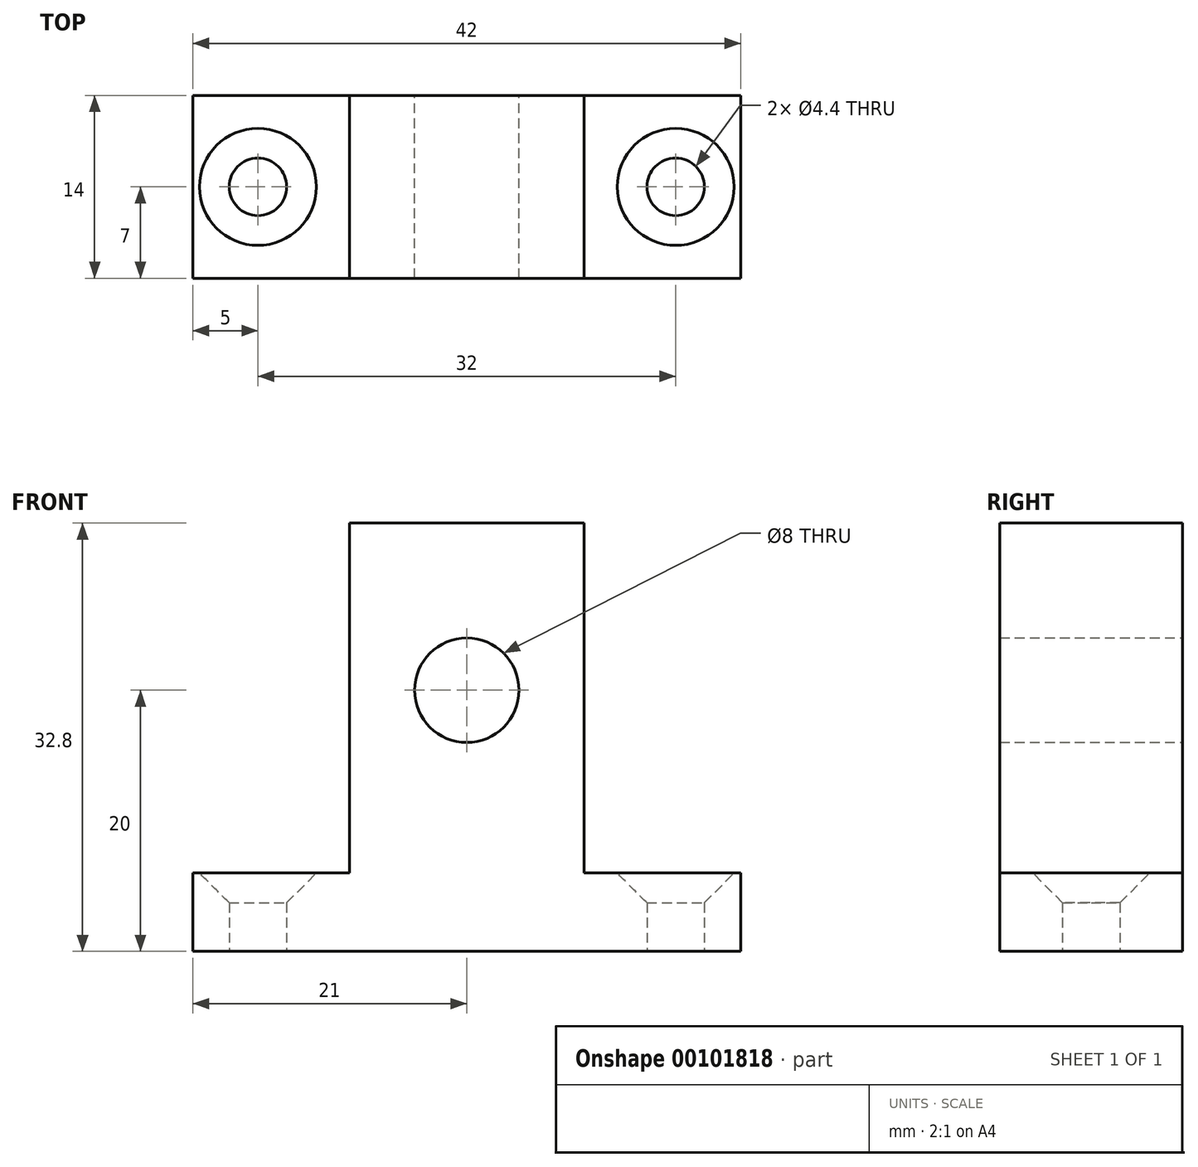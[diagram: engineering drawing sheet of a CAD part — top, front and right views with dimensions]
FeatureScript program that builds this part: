
annotation { "Feature Type Name" : "Feature", "Feature Type Description" : "" }
export const myFeature = defineFeature(function(context is Context, id is Id, definition is map)
    precondition{}
    {
        {
            var Q0;
            Q0=qCreatedBy(makeId("Top.planeOp"),FACE);
            var sketch = newSketch(context, id + "F0", { "sketchPlane" : qUnion([Q0])});
            skLineSegment(sketch, "E0.bottom", {"start": v(-21, 7) * mm, "end": v(21, 7) * mm});
            skLineSegment(sketch, "E0.top", {"start": v(-21, -7) * mm, "end": v(21, -7) * mm});
            skLineSegment(sketch, "E0.left", {"start": v(-21, 7) * mm, "end": v(-21, -7) * mm});
            skLineSegment(sketch, "E0.right", {"start": v(21, 7) * mm, "end": v(21, -7) * mm});
            skPoint(sketch, "E0.middle", {"position": v(0, 0) * mm});
            skSolve(sketch);
        }
        {
            var Q0;
            Q0 = qSketchRegion(id + "F0", true);
            extrude(context, id + "F1", {"entities" : qUnion([Q0]), "depth" : 6 * mm});
        }
        {
            var Q0;
            Q0=makeQuery(id+"F1.opExtrude","CAP_FACE",FACE,{"disambiguationData":[OSD([sQuery(id+"F0.wireOp",EDGE,"E0.bottom"),sQuery(id+"F0.wireOp",EDGE,"E0.top"),sQuery(id+"F0.wireOp",EDGE,"E0.left"),sQuery(id+"F0.wireOp",EDGE,"E0.right")])],"isStart":false});
            var sketch = newSketch(context, id + "F2", { "sketchPlane" : qUnion([Q0])});
            skLineSegment(sketch, "E1.bottom", {"start": v(-9, 7) * mm, "end": v(9, 7) * mm});
            skLineSegment(sketch, "E1.top", {"start": v(-9, -7) * mm, "end": v(9, -7) * mm});
            skLineSegment(sketch, "E1.left", {"start": v(-9, 7) * mm, "end": v(-9, -7) * mm});
            skLineSegment(sketch, "E1.right", {"start": v(9, 7) * mm, "end": v(9, -7) * mm});
            skPoint(sketch, "E1.middle", {"position": v(0, 0) * mm});
            skSolve(sketch);
        }
        {
            var Q0;
            Q0=makeQuery(id+"F2.imprint","IMPRINT",FACE,{"disambiguationData":[TD([[makeQuery(id+"F2.imprint","IMPRINT",EDGE,{"derivedFrom":sQuery(id+"F2.wireOp",EDGE,"E1.bottom")}),-1.0]])]});
            extrude(context, id + "F3", {"entities" : qUnion([Q0]), "operationType" : NewBodyOperationType.ADD, "depth" : (32.8 - 6) * mm});
        }
        {
            var Q0;
            {var subQ0=sQuery(id+"F0.wireOp",EDGE,"E0.left");var subQ1=sQuery(id+"F0.wireOp",EDGE,"E0.top");var subQ2=sQuery(id+"F0.wireOp",EDGE,"E0.bottom");Q0=makeQuery(id+"F3.boolean.opBoolean","SPLIT",FACE,{"disambiguationData":[TD([makeQuery(id+"F1.opExtrude","SWEPT_FACE",FACE,{"disambiguationData":[OSD([subQ0])]})])],"derivedFrom":makeQuery(id+"F1.opExtrude","CAP_FACE",FACE,{"disambiguationData":[OSD([subQ2,subQ1,subQ0,sQuery(id+"F0.wireOp",EDGE,"E0.right")])],"isStart":false})});}
            var sketch = newSketch(context, id + "F4", { "sketchPlane" : qUnion([Q0])});
            skPoint(sketch, "E2", {"position": v(-16, 0) * mm});
            skPoint(sketch, "E3.MirrorP", {"position": v(16, 0) * mm});
            skSolve(sketch);
        }
        {
            var Q0;
            Q0=makeQuery(id+"F3.boolean.opBoolean","MERGE",FACE,{"derivedFrom":[makeQuery(id+"F1.opExtrude","SWEPT_FACE",FACE,{"disambiguationData":[OSD([sQuery(id+"F0.wireOp",EDGE,"E0.top")])]}),makeQuery(id+"F3.opExtrude","SWEPT_FACE",FACE,{"disambiguationData":[OSD([sQuery(id+"F2.wireOp",EDGE,"E1.top")])]})]});
            var sketch = newSketch(context, id + "F5", { "sketchPlane" : qUnion([Q0])});
            skPoint(sketch, "E4", {"position": v(0, 20) * mm});
            skSolve(sketch);
        }
        {
            var Q0;
            Q0=sQuery(id+"F4.wireOp",VERTEX,"E2");
            var Q1;
            Q1=sQuery(id+"F4.wireOp",VERTEX,"E3.MirrorP");
            var Q2;
            Q2=makeQuery(id+"F1.opExtrude","SWEPT_BODY",BODY,{"disambiguationData":[OSD([sQuery(id+"F0.wireOp",EDGE,"E0.bottom"),sQuery(id+"F0.wireOp",EDGE,"E0.top"),sQuery(id+"F0.wireOp",EDGE,"E0.left"),sQuery(id+"F0.wireOp",EDGE,"E0.right")])]});
            hole(context, id + "F6", {"style" : HoleStyle.C_SINK, "endStyle" : HoleEndStyle.THROUGH, "standardTappedOrClearance" : lookupTablePath({ "standard" : "ISO", "fit" : "Normal", "size" : "M4", "type" : "Clearance" }), "standardBlindInLast" : lookupTablePath({ "fit" : "Standard", "standard" : "ISO", "size" : "M4", "type" : "Clearance" }), "holeDiameter" : 4.4 * mm, "cSinkDiameter" : 8.96 * mm, "cSinkAngle" : 90 * degree, "locations" : qUnion([Q0, Q1]), "scope" : qUnion([Q2]), "isTappedThrough" : true});
        }
        {
            var Q0;
            Q0=sQuery(id+"F5.wireOp",VERTEX,"E4");
            var Q1;
            Q1=makeQuery(id+"F1.opExtrude","SWEPT_BODY",BODY,{"disambiguationData":[OSD([sQuery(id+"F0.wireOp",EDGE,"E0.bottom"),sQuery(id+"F0.wireOp",EDGE,"E0.top"),sQuery(id+"F0.wireOp",EDGE,"E0.left"),sQuery(id+"F0.wireOp",EDGE,"E0.right")])]});
            hole(context, id + "F7", {"style" : HoleStyle.SIMPLE, "endStyle" : HoleEndStyle.THROUGH, "holeDiameter" : 8 * mm, "locations" : qUnion([Q0]), "scope" : qUnion([Q1]), "isTappedThrough" : true});
        }
    });
